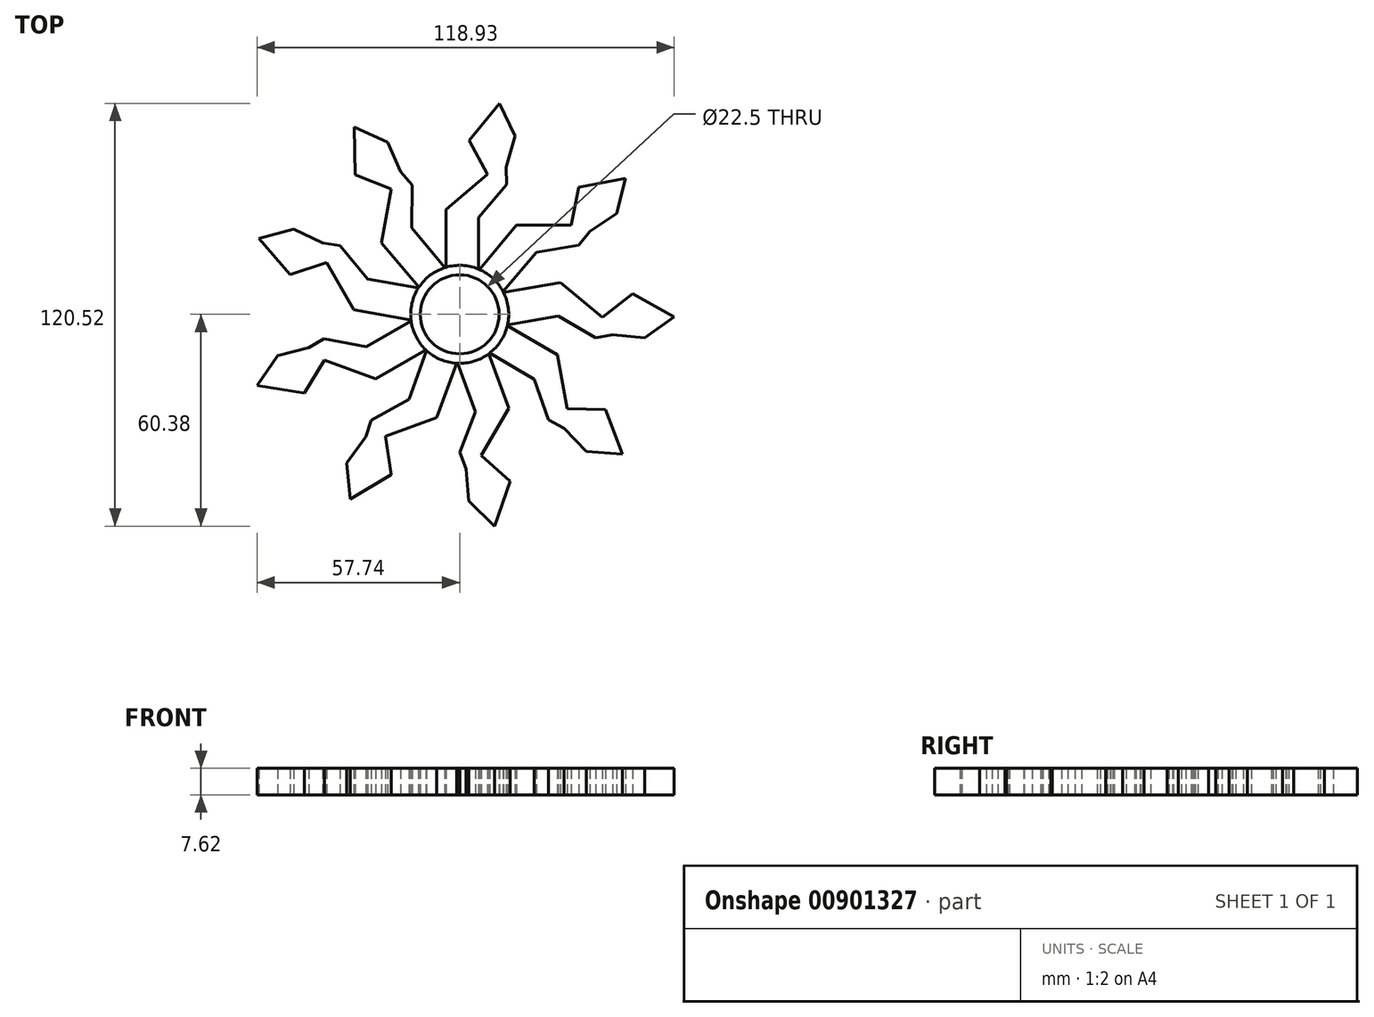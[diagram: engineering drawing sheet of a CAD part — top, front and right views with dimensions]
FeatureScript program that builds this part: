
annotation { "Feature Type Name" : "Feature", "Feature Type Description" : "" }
export const myFeature = defineFeature(function(context is Context, id is Id, definition is map)
    precondition{}
    {
        {
            var Q0;
            Q0=qCreatedBy(makeId("Top.planeOp"),FACE);
            var sketch = newSketch(context, id + "F0", { "sketchPlane" : qUnion([Q0])});
            skCircle(sketch, "E0", {"center": v(0, 0) * mm, "radius": 13.97 * mm});
            skCircle(sketch, "E1", {"center": v(0, 0) * mm, "radius": 11.25 * mm});
            skLineSegment(sketch, "E2", {"start": v(31.76, 25.47) * mm, "end": v(33.99, 36.2) * mm});
            skLineSegment(sketch, "E3", {"start": v(33.99, 36.2) * mm, "end": v(47.32, 38.8) * mm});
            skLineSegment(sketch, "E4", {"start": v(47.32, 38.8) * mm, "end": v(44.73, 28.8) * mm});
            skLineSegment(sketch, "E5", {"start": v(44.73, 28.8) * mm, "end": v(37.13, 23.61) * mm});
            skLineSegment(sketch, "E6", {"start": v(37.13, 23.61) * mm, "end": v(33.99, 19.73) * mm});
            skLineSegment(sketch, "E7", {"start": v(33.99, 19.73) * mm, "end": v(21.87, 17.74) * mm});
            skLineSegment(sketch, "E8", {"start": v(31.76, 25.47) * mm, "end": v(16.2, 25.47) * mm});
            skLineSegment(sketch, "E9", {"start": v(21.87, 17.74) * mm, "end": v(12.38, 6.48) * mm});
            skLineSegment(sketch, "E10", {"start": v(16.2, 25.47) * mm, "end": v(5.57, 12.76) * mm});
            skArc(sketch, "E11", {"start": v(12.38, 6.48) * mm, "mid": v(9.52, 10.21) * mm, "end": v(5.57, 12.76) * mm});
            skArc(sketch, "E12", {"start": v(12.38, 6.48) * mm, "mid": v(9.5, 10.18) * mm, "end": v(5.57, 12.76) * mm});
            skLineSegment(sketch, "E13.1.0", {"start": v(-3.96, 29.93) * mm, "end": v(-3.94, 13.36) * mm});
            skLineSegment(sketch, "E13.1.1", {"start": v(7.96, 39.93) * mm, "end": v(-3.96, 29.93) * mm});
            skLineSegment(sketch, "E13.1.2", {"start": v(7.96, 39.93) * mm, "end": v(2.76, 49.58) * mm});
            skLineSegment(sketch, "E13.1.3", {"start": v(2.76, 49.58) * mm, "end": v(11.3, 60.14) * mm});
            skLineSegment(sketch, "E13.1.4", {"start": v(15.75, 50.81) * mm, "end": v(13.27, 41.96) * mm});
            skLineSegment(sketch, "E13.1.5", {"start": v(11.3, 60.14) * mm, "end": v(15.75, 50.81) * mm});
            skLineSegment(sketch, "E13.1.6", {"start": v(13.35, 36.96) * mm, "end": v(5.35, 27.65) * mm});
            skLineSegment(sketch, "E13.1.7", {"start": v(13.27, 41.96) * mm, "end": v(13.35, 36.96) * mm});
            skLineSegment(sketch, "E13.1.8", {"start": v(5.35, 27.65) * mm, "end": v(5.32, 12.92) * mm});
            skArc(sketch, "E13.1.9", {"start": v(5.32, 12.92) * mm, "mid": v(0.73, 13.9) * mm, "end": v(-3.94, 13.36) * mm});
            skLineSegment(sketch, "E13.2.0", {"start": v(-22.27, 20.38) * mm, "end": v(-11.6, 7.7) * mm});
            skLineSegment(sketch, "E13.2.1", {"start": v(-19.56, 35.7) * mm, "end": v(-22.27, 20.38) * mm});
            skLineSegment(sketch, "E13.2.2", {"start": v(-19.56, 35.7) * mm, "end": v(-29.76, 39.76) * mm});
            skLineSegment(sketch, "E13.2.3", {"start": v(-29.76, 39.76) * mm, "end": v(-30, 53.34) * mm});
            skLineSegment(sketch, "E13.2.4", {"start": v(-20.6, 49.05) * mm, "end": v(-16.8, 40.67) * mm});
            skLineSegment(sketch, "E13.2.5", {"start": v(-30, 53.34) * mm, "end": v(-20.6, 49.05) * mm});
            skLineSegment(sketch, "E13.2.6", {"start": v(-13.53, 36.9) * mm, "end": v(-13.68, 24.62) * mm});
            skLineSegment(sketch, "E13.2.7", {"start": v(-16.8, 40.67) * mm, "end": v(-13.53, 36.9) * mm});
            skLineSegment(sketch, "E13.2.8", {"start": v(-13.68, 24.62) * mm, "end": v(-4.23, 13.32) * mm});
            skArc(sketch, "E13.2.9", {"start": v(-4.23, 13.32) * mm, "mid": v(-8.38, 11.12) * mm, "end": v(-11.6, 7.7) * mm});
            skLineSegment(sketch, "E13.3.0", {"start": v(-30.16, 1.3) * mm, "end": v(-13.84, -1.56) * mm});
            skLineSegment(sketch, "E13.3.1", {"start": v(-37.94, 14.77) * mm, "end": v(-30.16, 1.3) * mm});
            skLineSegment(sketch, "E13.3.2", {"start": v(-37.94, 14.77) * mm, "end": v(-48.35, 11.33) * mm});
            skLineSegment(sketch, "E13.3.3", {"start": v(-48.35, 11.33) * mm, "end": v(-57.26, 21.58) * mm});
            skLineSegment(sketch, "E13.3.4", {"start": v(-47.3, 24.34) * mm, "end": v(-39.02, 20.35) * mm});
            skLineSegment(sketch, "E13.3.5", {"start": v(-57.26, 21.58) * mm, "end": v(-47.3, 24.34) * mm});
            skLineSegment(sketch, "E13.3.6", {"start": v(-34.08, 19.57) * mm, "end": v(-26.3, 10.07) * mm});
            skLineSegment(sketch, "E13.3.7", {"start": v(-39.02, 20.35) * mm, "end": v(-34.08, 19.57) * mm});
            skLineSegment(sketch, "E13.3.8", {"start": v(-26.3, 10.07) * mm, "end": v(-11.8, 7.48) * mm});
            skArc(sketch, "E13.3.9", {"start": v(-11.8, 7.48) * mm, "mid": v(-13.56, 3.13) * mm, "end": v(-13.84, -1.56) * mm});
            skLineSegment(sketch, "E13.4.0", {"start": v(-23.94, -18.39) * mm, "end": v(-9.6, -10.09) * mm});
            skLineSegment(sketch, "E13.4.1", {"start": v(-38.56, -13.07) * mm, "end": v(-23.94, -18.39) * mm});
            skLineSegment(sketch, "E13.4.2", {"start": v(-38.56, -13.07) * mm, "end": v(-44.32, -22.4) * mm});
            skLineSegment(sketch, "E13.4.3", {"start": v(-44.32, -22.4) * mm, "end": v(-57.74, -20.28) * mm});
            skLineSegment(sketch, "E13.4.4", {"start": v(-51.88, -11.77) * mm, "end": v(-42.97, -9.49) * mm});
            skLineSegment(sketch, "E13.4.5", {"start": v(-57.74, -20.28) * mm, "end": v(-51.88, -11.77) * mm});
            skLineSegment(sketch, "E13.4.6", {"start": v(-38.68, -6.92) * mm, "end": v(-26.62, -9.2) * mm});
            skLineSegment(sketch, "E13.4.7", {"start": v(-42.97, -9.49) * mm, "end": v(-38.68, -6.92) * mm});
            skLineSegment(sketch, "E13.4.8", {"start": v(-26.62, -9.2) * mm, "end": v(-13.85, -1.85) * mm});
            skArc(sketch, "E13.4.9", {"start": v(-13.85, -1.85) * mm, "mid": v(-12.4, -6.32) * mm, "end": v(-9.6, -10.09) * mm});
            skLineSegment(sketch, "E13.5.0", {"start": v(-6.52, -29.47) * mm, "end": v(-0.87, -13.9) * mm});
            skLineSegment(sketch, "E13.5.1", {"start": v(-21.14, -34.8) * mm, "end": v(-6.52, -29.47) * mm});
            skLineSegment(sketch, "E13.5.2", {"start": v(-21.14, -34.8) * mm, "end": v(-19.55, -45.65) * mm});
            skLineSegment(sketch, "E13.5.3", {"start": v(-19.55, -45.65) * mm, "end": v(-31.2, -52.65) * mm});
            skLineSegment(sketch, "E13.5.4", {"start": v(-32.18, -42.36) * mm, "end": v(-26.82, -34.9) * mm});
            skLineSegment(sketch, "E13.5.5", {"start": v(-31.2, -52.65) * mm, "end": v(-32.18, -42.36) * mm});
            skLineSegment(sketch, "E13.5.6", {"start": v(-25.19, -30.17) * mm, "end": v(-14.49, -24.16) * mm});
            skLineSegment(sketch, "E13.5.7", {"start": v(-26.82, -34.9) * mm, "end": v(-25.19, -30.17) * mm});
            skLineSegment(sketch, "E13.5.8", {"start": v(-14.49, -24.16) * mm, "end": v(-9.42, -10.32) * mm});
            skArc(sketch, "E13.5.9", {"start": v(-9.42, -10.32) * mm, "mid": v(-5.44, -12.81) * mm, "end": v(-0.87, -13.9) * mm});
            skLineSegment(sketch, "E13.6.0", {"start": v(13.95, -26.77) * mm, "end": v(8.27, -11.2) * mm});
            skLineSegment(sketch, "E13.6.1", {"start": v(6.17, -40.24) * mm, "end": v(13.95, -26.77) * mm});
            skLineSegment(sketch, "E13.6.2", {"start": v(6.17, -40.24) * mm, "end": v(14.36, -47.54) * mm});
            skLineSegment(sketch, "E13.6.3", {"start": v(14.36, -47.54) * mm, "end": v(9.94, -60.38) * mm});
            skLineSegment(sketch, "E13.6.4", {"start": v(2.58, -53.14) * mm, "end": v(1.88, -43.97) * mm});
            skLineSegment(sketch, "E13.6.5", {"start": v(9.94, -60.38) * mm, "end": v(2.58, -53.14) * mm});
            skLineSegment(sketch, "E13.6.6", {"start": v(0.1, -39.3) * mm, "end": v(4.43, -27.82) * mm});
            skLineSegment(sketch, "E13.6.7", {"start": v(1.88, -43.97) * mm, "end": v(0.1, -39.3) * mm});
            skLineSegment(sketch, "E13.6.8", {"start": v(4.43, -27.82) * mm, "end": v(-0.58, -13.96) * mm});
            skArc(sketch, "E13.6.9", {"start": v(-0.58, -13.96) * mm, "mid": v(4.07, -13.31) * mm, "end": v(8.27, -11.2) * mm});
            skLineSegment(sketch, "E13.7.0", {"start": v(27.9, -11.54) * mm, "end": v(13.54, -3.27) * mm});
            skLineSegment(sketch, "E13.7.1", {"start": v(30.6, -26.86) * mm, "end": v(27.9, -11.54) * mm});
            skLineSegment(sketch, "E13.7.2", {"start": v(30.6, -26.86) * mm, "end": v(41.56, -27.18) * mm});
            skLineSegment(sketch, "E13.7.3", {"start": v(41.56, -27.18) * mm, "end": v(46.43, -39.86) * mm});
            skLineSegment(sketch, "E13.7.4", {"start": v(36.13, -39.05) * mm, "end": v(29.7, -32.47) * mm});
            skLineSegment(sketch, "E13.7.5", {"start": v(46.43, -39.86) * mm, "end": v(36.13, -39.05) * mm});
            skLineSegment(sketch, "E13.7.6", {"start": v(25.33, -30.04) * mm, "end": v(21.27, -18.46) * mm});
            skLineSegment(sketch, "E13.7.7", {"start": v(29.7, -32.47) * mm, "end": v(25.33, -30.04) * mm});
            skLineSegment(sketch, "E13.7.8", {"start": v(21.27, -18.46) * mm, "end": v(8.53, -11.07) * mm});
            skArc(sketch, "E13.7.9", {"start": v(8.53, -11.07) * mm, "mid": v(11.68, -7.58) * mm, "end": v(13.54, -3.27) * mm});
            skLineSegment(sketch, "E13.8.0", {"start": v(28.78, 9.1) * mm, "end": v(12.47, 6.2) * mm});
            skLineSegment(sketch, "E13.8.1", {"start": v(40.7, -0.9) * mm, "end": v(28.78, 9.1) * mm});
            skLineSegment(sketch, "E13.8.2", {"start": v(40.7, -0.9) * mm, "end": v(49.3, 5.9) * mm});
            skLineSegment(sketch, "E13.8.3", {"start": v(49.3, 5.9) * mm, "end": v(61.2, -0.7) * mm});
            skLineSegment(sketch, "E13.8.4", {"start": v(52.78, -6.69) * mm, "end": v(43.63, -5.78) * mm});
            skLineSegment(sketch, "E13.8.5", {"start": v(61.2, -0.7) * mm, "end": v(52.78, -6.69) * mm});
            skLineSegment(sketch, "E13.8.6", {"start": v(38.72, -6.73) * mm, "end": v(28.16, -0.47) * mm});
            skLineSegment(sketch, "E13.8.7", {"start": v(43.63, -5.78) * mm, "end": v(38.72, -6.73) * mm});
            skLineSegment(sketch, "E13.8.8", {"start": v(28.16, -0.47) * mm, "end": v(13.64, -3) * mm});
            skArc(sketch, "E13.8.9", {"start": v(13.64, -3) * mm, "mid": v(13.82, 1.7) * mm, "end": v(12.47, 6.2) * mm});
            skSolve(sketch);
        }
        {
            var Q0;
            {var subQ0=sQuery(id+"F0.wireOp",EDGE,"E13.1.1");Q0=makeQuery(id+"F0.imprint","IMPRINT",FACE,{"disambiguationData":[TD([[makeQuery(id+"F0.imprint","IMPRINT",EDGE,{"derivedFrom":subQ0}),1.0]])]});}
            var Q1;
            {var subQ0=sQuery(id+"F0.wireOp",EDGE,"E13.2.1");Q1=makeQuery(id+"F0.imprint","IMPRINT",FACE,{"disambiguationData":[TD([[makeQuery(id+"F0.imprint","IMPRINT",EDGE,{"derivedFrom":subQ0}),1.0]])]});}
            var Q2;
            Q2=makeQuery(id+"F0.imprint","IMPRINT",FACE,{"disambiguationData":[TD([[makeQuery(id+"F0.imprint","IMPRINT",EDGE,{"derivedFrom":sQuery(id+"F0.wireOp",EDGE,"E2")}),-1.0]])]});
            var Q3;
            {var subQ0=sQuery(id+"F0.wireOp",EDGE,"E13.8.1");Q3=makeQuery(id+"F0.imprint","IMPRINT",FACE,{"disambiguationData":[TD([[makeQuery(id+"F0.imprint","IMPRINT",EDGE,{"derivedFrom":subQ0}),1.0]])]});}
            var Q4;
            {var subQ0=sQuery(id+"F0.wireOp",EDGE,"E13.7.1");Q4=makeQuery(id+"F0.imprint","IMPRINT",FACE,{"disambiguationData":[TD([[makeQuery(id+"F0.imprint","IMPRINT",EDGE,{"derivedFrom":subQ0}),1.0]])]});}
            var Q5;
            {var subQ4=sQuery(id+"F0.wireOp",EDGE,"E13.6.1");Q5=makeQuery(id+"F0.imprint","IMPRINT",FACE,{"disambiguationData":[TD([[makeQuery(id+"F0.imprint","IMPRINT",EDGE,{"derivedFrom":subQ4}),1.0]])]});}
            var Q6;
            {var subQ0=sQuery(id+"F0.wireOp",EDGE,"E13.5.1");Q6=makeQuery(id+"F0.imprint","IMPRINT",FACE,{"disambiguationData":[TD([[makeQuery(id+"F0.imprint","IMPRINT",EDGE,{"derivedFrom":subQ0}),1.0]])]});}
            var Q7;
            {var subQ0=sQuery(id+"F0.wireOp",EDGE,"E13.4.1");Q7=makeQuery(id+"F0.imprint","IMPRINT",FACE,{"disambiguationData":[TD([[makeQuery(id+"F0.imprint","IMPRINT",EDGE,{"derivedFrom":subQ0}),1.0]])]});}
            var Q8;
            {var subQ0=sQuery(id+"F0.wireOp",EDGE,"E13.3.1");Q8=makeQuery(id+"F0.imprint","IMPRINT",FACE,{"disambiguationData":[TD([[makeQuery(id+"F0.imprint","IMPRINT",EDGE,{"derivedFrom":subQ0}),1.0]])]});}
            extrude(context, id + "F1", {"entities" : qUnion([Q0, Q1, Q2, Q3, Q4, Q5, Q6, Q7, Q8]), "depth" : 7.62 * mm, "offsetDistance" : 25.4 * mm});
        }
        {
            var Q0;
            Q0 = qSketchRegion(id + "F0", true);
            extrude(context, id + "F2", {"entities" : qUnion([Q0]), "depth" : 7.62 * mm, "offsetDistance" : 25.4 * mm});
        }
    });
